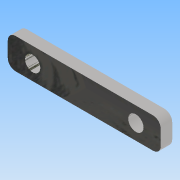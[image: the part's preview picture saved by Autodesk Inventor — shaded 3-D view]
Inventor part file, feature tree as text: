
AUTODESK INVENTOR PART (.ipt)
format: ipt  version: 2015 (Build 190159000, 159)  size: 100,352 bytes
history: native  units: mm
features: extrude x1, fillet x1, sketch x1
ambient origin geometry x8: Origin, YZ Plane, XZ Plane, XY Plane, X Axis, Y Axis, Z Axis, Center Point
bodies: Solide1 (feature_tree)
feature tree (3):
  extrude  "Extrusion1"  Depth=8.0mm
  fillet  "Congé1"  Radius=40.0mm
  sketch  "Esquisse1"
